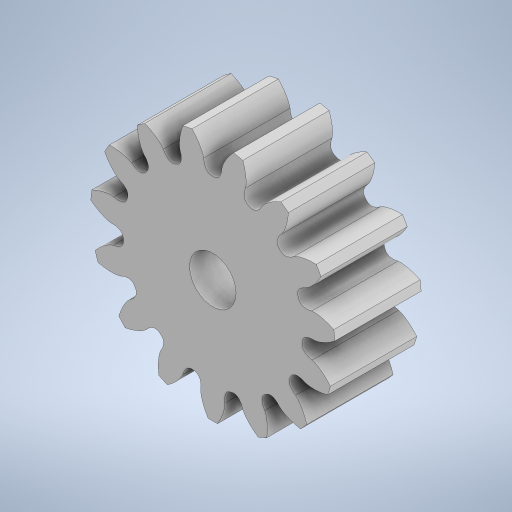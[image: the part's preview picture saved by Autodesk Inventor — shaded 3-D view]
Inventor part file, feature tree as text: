
AUTODESK INVENTOR PART (.ipt)
format: ipt  version: 2023 (Build 270158000, 158)  size: 394,752 bytes
history: native  units: mm
features: sketch x2, extrude x2, pattern_circular x1, hole x1
ambient origin geometry x8: Origin, YZ Plane, XZ Plane, XY Plane, X Axis, Y Axis, Z Axis, Center Point
bodies: Solid1 (feature_tree)
feature tree (6):
  sketch  "Sketch1"  dims[d0=12.0mm d1=0.0mm]
  extrude  "Extrusion1"  TaperAngle=0.0deg  [1 undecoded]
  extrude  "Extrusion2"  Depth=150.0mm TaperAngle=360.0deg
  pattern_circular  "Circular Pattern2"  [2 undecoded]
  hole  "Hole1"  [1 undecoded]
  sketch  "Sketch2"  dims[d2=0.0mm d3=0.0mm d7=150.0mm d8=360.0deg d10=6.469mm d11=6.0mm d12=8.0mm d13=2.0mm d14=90.0deg d15=8.0mm d16=20.594885mm]
note: 4 required parameter values undecoded (feature->parameter linkage not recoverable at this tier; creation-order binding heuristic only, values carry confidence <= 0.55)
